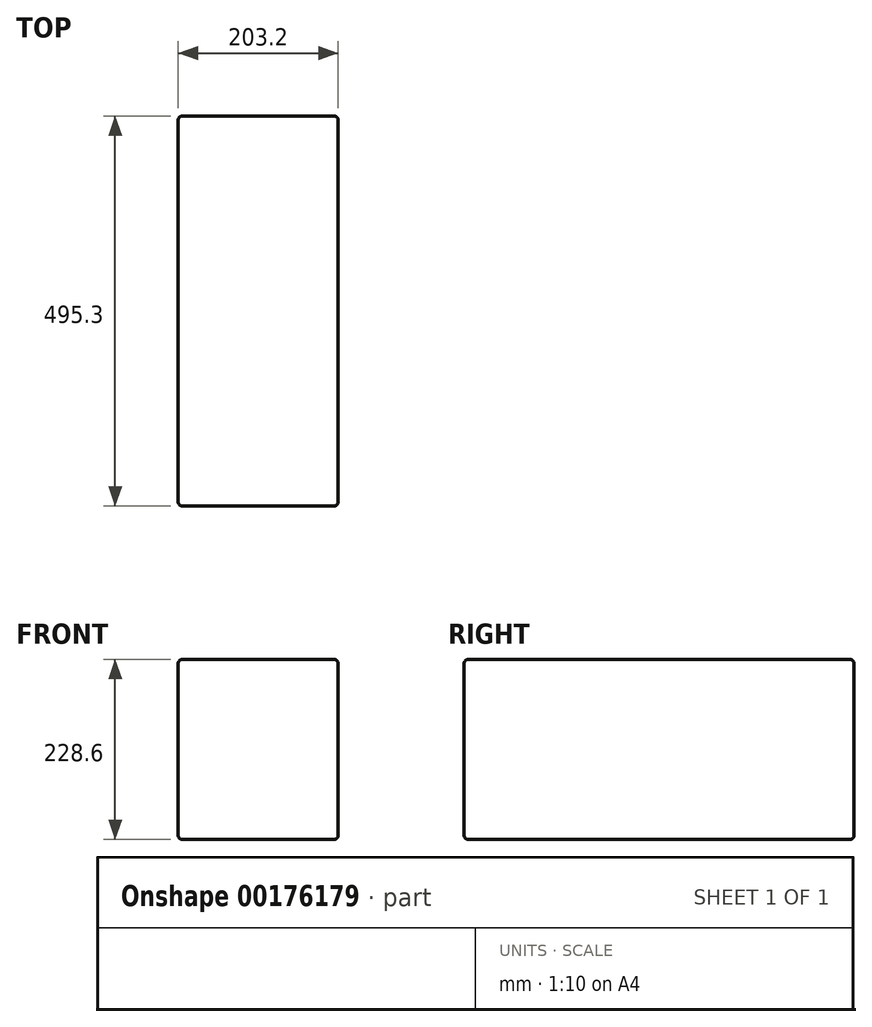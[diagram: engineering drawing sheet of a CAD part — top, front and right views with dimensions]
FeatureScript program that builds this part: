
annotation { "Feature Type Name" : "Feature", "Feature Type Description" : "" }
export const myFeature = defineFeature(function(context is Context, id is Id, definition is map)
    precondition{}
    {
        {
            var Q0;
            Q0=qCreatedBy(makeId("Front.planeOp"),FACE);
            var sketch = newSketch(context, id + "F0", { "sketchPlane" : qUnion([Q0])});
            skLineSegment(sketch, "E0.bottom", {"start": v(-101.6, 114.3) * mm, "end": v(101.6, 114.3) * mm});
            skLineSegment(sketch, "E0.top", {"start": v(-101.6, -114.3) * mm, "end": v(101.6, -114.3) * mm});
            skLineSegment(sketch, "E0.left", {"start": v(-101.6, 114.3) * mm, "end": v(-101.6, -114.3) * mm});
            skLineSegment(sketch, "E0.right", {"start": v(101.6, 114.3) * mm, "end": v(101.6, -114.3) * mm});
            skPoint(sketch, "E0.middle", {"position": v(0, 0) * mm});
            skSolve(sketch);
        }
        {
            var Q0;
            Q0 = qSketchRegion(id + "F0", true);
            extrude(context, id + "F1", {"entities" : qUnion([Q0]), "oppositeDirection" : true, "depth" : 495.3 * mm});
        }
        {
            var Q0;
            Q0=makeQuery(id+"F1.opExtrude","SWEPT_EDGE",EDGE,{"disambiguationData":[OSD([sQuery(id+"F0.wireOp",EDGE,"E0.bottom"),sQuery(id+"F0.wireOp",EDGE,"E0.right")])]});
            fillet(context, id + "F2", {"entities" : qUnion([Q0]), "radius" : 5.08 * mm, "tangentPropagation" : true, "allowEdgeOverflow" : false});
        }
        {
            var Q0;
            Q0=makeQuery(id+"F1.opExtrude","SWEPT_EDGE",EDGE,{"disambiguationData":[OSD([sQuery(id+"F0.wireOp",EDGE,"E0.bottom"),sQuery(id+"F0.wireOp",EDGE,"E0.left")])]});
            fillet(context, id + "F3", {"entities" : qUnion([Q0]), "radius" : 5.08 * mm, "tangentPropagation" : true, "allowEdgeOverflow" : false});
        }
        {
            var Q0;
            Q0=makeQuery(id+"F1.opExtrude","SWEPT_EDGE",EDGE,{"disambiguationData":[OSD([sQuery(id+"F0.wireOp",EDGE,"E0.top"),sQuery(id+"F0.wireOp",EDGE,"E0.right")])]});
            fillet(context, id + "F4", {"entities" : qUnion([Q0]), "radius" : 5.08 * mm, "tangentPropagation" : true, "allowEdgeOverflow" : false});
        }
        {
            var Q0;
            Q0=makeQuery(id+"F1.opExtrude","SWEPT_EDGE",EDGE,{"disambiguationData":[OSD([sQuery(id+"F0.wireOp",EDGE,"E0.top"),sQuery(id+"F0.wireOp",EDGE,"E0.left")])]});
            fillet(context, id + "F5", {"entities" : qUnion([Q0]), "radius" : 5.08 * mm, "tangentPropagation" : true, "allowEdgeOverflow" : false});
        }
        {
            var Q0;
            Q0=makeQuery(id+"F1.opExtrude","CAP_EDGE",EDGE,{"disambiguationData":[OSD([sQuery(id+"F0.wireOp",EDGE,"E0.bottom")])],"isStart":true});
            fillet(context, id + "F6", {"entities" : qUnion([Q0]), "radius" : 5.08 * mm, "tangentPropagation" : true, "allowEdgeOverflow" : false});
        }
        {
            var Q0;
            Q0=makeQuery(id+"F1.opExtrude","CAP_EDGE",EDGE,{"disambiguationData":[OSD([sQuery(id+"F0.wireOp",EDGE,"E0.bottom")])],"isStart":false});
            fillet(context, id + "F7", {"entities" : qUnion([Q0]), "radius" : 5.08 * mm, "tangentPropagation" : true, "allowEdgeOverflow" : false});
        }
    });
